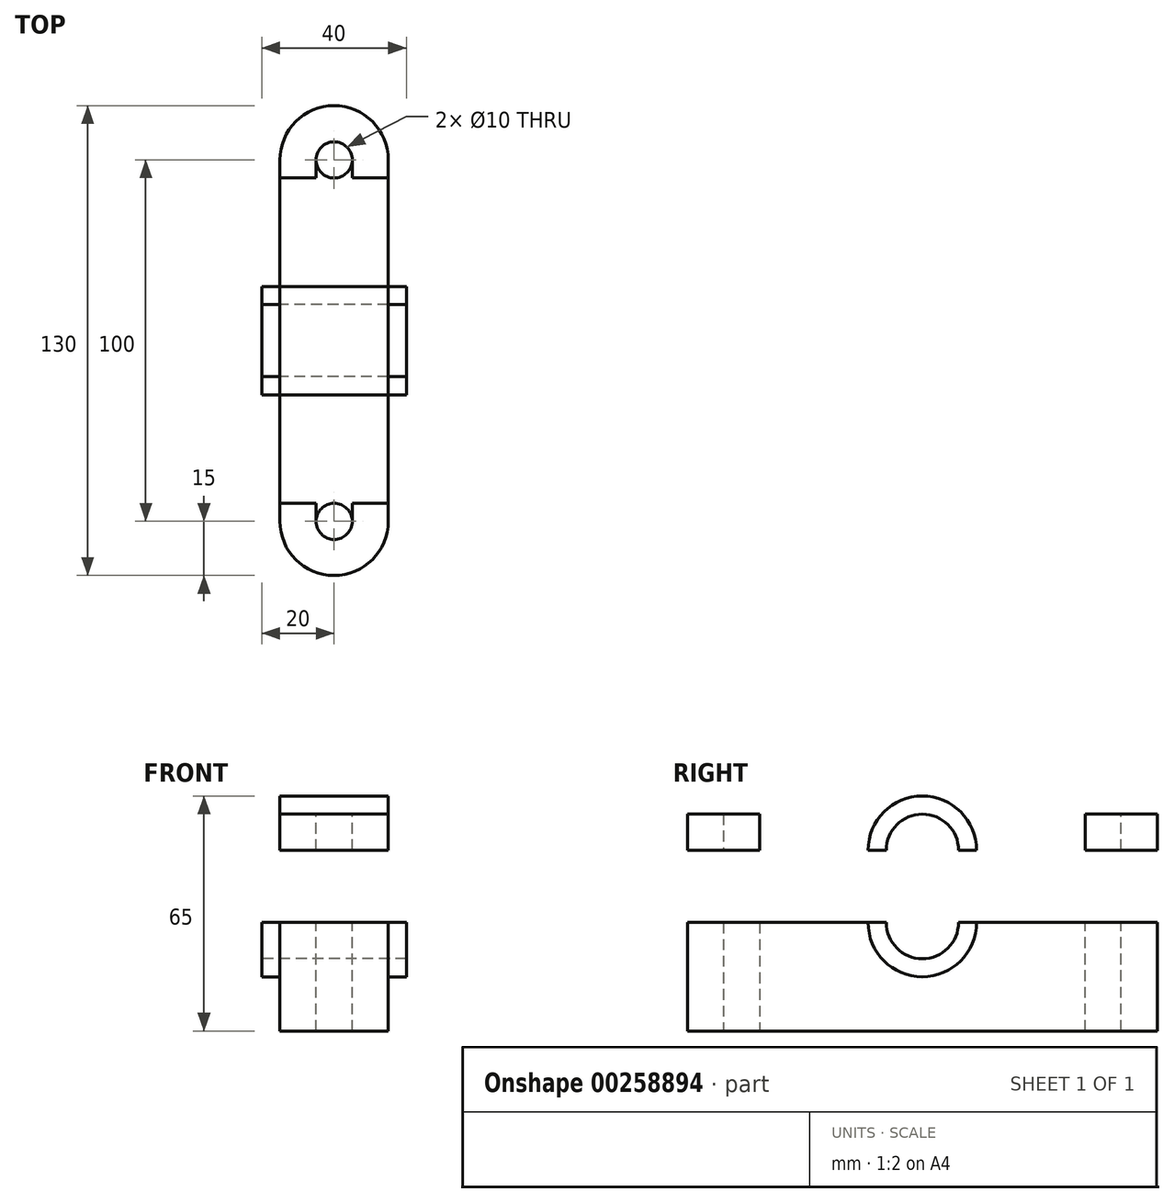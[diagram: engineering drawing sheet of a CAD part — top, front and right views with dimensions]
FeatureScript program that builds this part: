
annotation { "Feature Type Name" : "Feature", "Feature Type Description" : "" }
export const myFeature = defineFeature(function(context is Context, id is Id, definition is map)
    precondition{}
    {
        {
            var Q0;
            Q0=qCreatedBy(makeId("Right.planeOp"),FACE);
            var sketch = newSketch(context, id + "F0", { "sketchPlane" : qUnion([Q0])});
            skLineSegment(sketch, "E0", {"start": v(-65, 0) * mm, "end": v(-65, 30) * mm});
            skLineSegment(sketch, "E1", {"start": v(65, 0) * mm, "end": v(65, 30) * mm});
            skLineSegment(sketch, "E2", {"start": v(-50, 0) * mm, "end": v(-50, 30) * mm, "construction": true});
            skLineSegment(sketch, "E3", {"start": v(50, 0) * mm, "end": v(50, 30) * mm, "construction": true});
            skLineSegment(sketch, "E4.0", {"start": v(-45, 0) * mm, "end": v(-45, 30) * mm});
            skLineSegment(sketch, "E5.0", {"start": v(-55, 0) * mm, "end": v(-55, 30) * mm});
            skLineSegment(sketch, "E6.0", {"start": v(55, 0) * mm, "end": v(55, 30) * mm});
            skLineSegment(sketch, "E7.0", {"start": v(45, 0) * mm, "end": v(45, 30) * mm});
            skLineSegment(sketch, "E8", {"start": v(0, 0) * mm, "end": v(-45, 0) * mm});
            skLineSegment(sketch, "E9", {"start": v(-50, 0) * mm, "end": v(-45, 0) * mm});
            skLineSegment(sketch, "E10", {"start": v(-55, 0) * mm, "end": v(-50, 0) * mm});
            skLineSegment(sketch, "E11", {"start": v(-55, 0) * mm, "end": v(-65, 0) * mm});
            skLineSegment(sketch, "E12", {"start": v(-65, 30) * mm, "end": v(-55, 30) * mm});
            skLineSegment(sketch, "E13", {"start": v(-50, 30) * mm, "end": v(-55, 30) * mm});
            skLineSegment(sketch, "E14", {"start": v(-45, 30) * mm, "end": v(-50, 30) * mm});
            skLineSegment(sketch, "E15", {"start": v(-45, 30) * mm, "end": v(-15, 30) * mm});
            skArc(sketch, "E16", {"start": v(-10, 30) * mm, "mid": v(0, 20) * mm, "end": v(10, 30) * mm});
            skArc(sketch, "E17", {"start": v(-15, 30) * mm, "mid": v(0, 15) * mm, "end": v(15, 30) * mm});
            skLineSegment(sketch, "E18", {"start": v(-15, 30) * mm, "end": v(-10, 30) * mm});
            skLineSegment(sketch, "E19", {"start": v(10, 30) * mm, "end": v(15, 30) * mm});
            skLineSegment(sketch, "E20", {"start": v(15, 30) * mm, "end": v(45, 30) * mm});
            skLineSegment(sketch, "E21", {"start": v(50, 30) * mm, "end": v(45, 30) * mm});
            skLineSegment(sketch, "E22", {"start": v(55, 30) * mm, "end": v(50, 30) * mm});
            skLineSegment(sketch, "E23", {"start": v(55, 30) * mm, "end": v(65, 30) * mm});
            skLineSegment(sketch, "E24", {"start": v(55, 0) * mm, "end": v(65, 0) * mm});
            skLineSegment(sketch, "E25", {"start": v(50, 0) * mm, "end": v(55, 0) * mm});
            skLineSegment(sketch, "E26", {"start": v(45, 0) * mm, "end": v(50, 0) * mm});
            skLineSegment(sketch, "E27", {"start": v(0, 0) * mm, "end": v(45, 0) * mm});
            skArc(sketch, "E28", {"start": v(-10, 50) * mm, "mid": v(0, 60) * mm, "end": v(10, 50) * mm});
            skArc(sketch, "E29", {"start": v(-15, 50) * mm, "mid": v(0, 65) * mm, "end": v(15, 50) * mm});
            skLineSegment(sketch, "E30", {"start": v(-15, 50) * mm, "end": v(-10, 50) * mm});
            skLineSegment(sketch, "E31", {"start": v(10, 50) * mm, "end": v(15, 50) * mm});
            skArc(sketch, "E32", {"start": v(-28.28, 60) * mm, "mid": v(0, 80) * mm, "end": v(28.28, 60) * mm});
            skLineSegment(sketch, "E33", {"start": v(15, 50) * mm, "end": v(45, 50) * mm});
            skLineSegment(sketch, "E34", {"start": v(45, 50) * mm, "end": v(55, 50) * mm});
            skLineSegment(sketch, "E35", {"start": v(55, 50) * mm, "end": v(65, 50) * mm});
            skLineSegment(sketch, "E36", {"start": v(65, 50) * mm, "end": v(65, 60) * mm});
            skLineSegment(sketch, "E37", {"start": v(-15, 50) * mm, "end": v(-45, 50) * mm});
            skLineSegment(sketch, "E38", {"start": v(-45, 50) * mm, "end": v(-55, 50) * mm});
            skLineSegment(sketch, "E39", {"start": v(-55, 50) * mm, "end": v(-65, 50) * mm});
            skLineSegment(sketch, "E40", {"start": v(-65, 50) * mm, "end": v(-65, 60) * mm});
            skLineSegment(sketch, "E41", {"start": v(55, 50) * mm, "end": v(55, 60) * mm});
            skLineSegment(sketch, "E42", {"start": v(55, 60) * mm, "end": v(65, 60) * mm});
            skLineSegment(sketch, "E43", {"start": v(45, 50) * mm, "end": v(45, 60) * mm});
            skLineSegment(sketch, "E44", {"start": v(45, 60) * mm, "end": v(55, 60) * mm});
            skLineSegment(sketch, "E45", {"start": v(45, 60) * mm, "end": v(28.28, 60) * mm});
            skLineSegment(sketch, "E46", {"start": v(-55, 50) * mm, "end": v(-55, 60) * mm});
            skLineSegment(sketch, "E47", {"start": v(-55, 60) * mm, "end": v(-65, 60) * mm});
            skLineSegment(sketch, "E48", {"start": v(-45, 50) * mm, "end": v(-45, 60) * mm});
            skLineSegment(sketch, "E49", {"start": v(-45, 60) * mm, "end": v(-55, 60) * mm});
            skLineSegment(sketch, "E50", {"start": v(-45, 60) * mm, "end": v(-28.28, 60) * mm});
            skSolve(sketch);
        }
        {
            var Q0;
            Q0=makeQuery(id+"F0.imprint","IMPRINT",FACE,{"disambiguationData":[TD([[makeQuery(id+"F0.imprint","IMPRINT",EDGE,{"derivedFrom":sQuery(id+"F0.wireOp",EDGE,"E28")}),1.0]])]});
            var Q1;
            Q1=makeQuery(id+"F0.imprint","IMPRINT",FACE,{"disambiguationData":[TD([[makeQuery(id+"F0.imprint","IMPRINT",EDGE,{"derivedFrom":sQuery(id+"F0.wireOp",EDGE,"E16")}),-1.0]])]});
            extrude(context, id + "F1", {"entities" : qUnion([Q0, Q1]), "depth" : 40 * mm, "symmetric" : true});
        }
        {
            var Q0;
            Q0=makeQuery(id+"F0.imprint","IMPRINT",FACE,{"disambiguationData":[TD([[makeQuery(id+"F0.imprint","IMPRINT",EDGE,{"derivedFrom":sQuery(id+"F0.wireOp",EDGE,"E39")}),-1.0]])]});
            var Q1;
            Q1=makeQuery(id+"F0.imprint","IMPRINT",FACE,{"disambiguationData":[TD([[makeQuery(id+"F0.imprint","IMPRINT",EDGE,{"derivedFrom":sQuery(id+"F0.wireOp",EDGE,"E29")}),1.0]])]});
            var Q2;
            Q2=makeQuery(id+"F0.imprint","IMPRINT",FACE,{"disambiguationData":[TD([[makeQuery(id+"F0.imprint","IMPRINT",EDGE,{"derivedFrom":sQuery(id+"F0.wireOp",EDGE,"E38")}),-1.0]])]});
            var Q3;
            Q3=makeQuery(id+"F0.imprint","IMPRINT",FACE,{"disambiguationData":[TD([[makeQuery(id+"F0.imprint","IMPRINT",EDGE,{"derivedFrom":sQuery(id+"F0.wireOp",EDGE,"E34")}),1.0]])]});
            var Q4;
            Q4=makeQuery(id+"F0.imprint","IMPRINT",FACE,{"disambiguationData":[TD([[makeQuery(id+"F0.imprint","IMPRINT",EDGE,{"derivedFrom":sQuery(id+"F0.wireOp",EDGE,"E35")}),1.0]])]});
            var Q5;
            Q5=makeQuery(id+"F0.imprint","IMPRINT",FACE,{"disambiguationData":[TD([[makeQuery(id+"F0.imprint","IMPRINT",EDGE,{"derivedFrom":sQuery(id+"F0.wireOp",EDGE,"E4.0")}),-1.0]])]});
            var Q6;
            Q6=makeQuery(id+"F0.imprint","IMPRINT",FACE,{"disambiguationData":[TD([[makeQuery(id+"F0.imprint","IMPRINT",EDGE,{"derivedFrom":sQuery(id+"F0.wireOp",EDGE,"E6.0")}),1.0]])]});
            var Q7;
            Q7=makeQuery(id+"F0.imprint","IMPRINT",FACE,{"disambiguationData":[TD([[makeQuery(id+"F0.imprint","IMPRINT",EDGE,{"derivedFrom":sQuery(id+"F0.wireOp",EDGE,"E1")}),1.0]])]});
            var Q8;
            Q8=makeQuery(id+"F0.imprint","IMPRINT",FACE,{"disambiguationData":[TD([[makeQuery(id+"F0.imprint","IMPRINT",EDGE,{"derivedFrom":sQuery(id+"F0.wireOp",EDGE,"E4.0")}),1.0]])]});
            var Q9;
            Q9=makeQuery(id+"F0.imprint","IMPRINT",FACE,{"disambiguationData":[TD([[makeQuery(id+"F0.imprint","IMPRINT",EDGE,{"derivedFrom":sQuery(id+"F0.wireOp",EDGE,"E0")}),-1.0]])]});
            extrude(context, id + "F2", {"entities" : qUnion([Q0, Q1, Q2, Q3, Q4, Q5, Q6, Q7, Q8, Q9]), "operationType" : NewBodyOperationType.ADD, "depth" : 30 * mm, "symmetric" : true});
        }
        {
            var Q0;
            Q0=makeQuery(id+"F0.imprint","IMPRINT",FACE,{"disambiguationData":[TD([[makeQuery(id+"F0.imprint","IMPRINT",EDGE,{"derivedFrom":sQuery(id+"F0.wireOp",EDGE,"E38")}),-1.0]])]});
            var Q1;
            Q1=makeQuery(id+"F0.imprint","IMPRINT",FACE,{"disambiguationData":[TD([[makeQuery(id+"F0.imprint","IMPRINT",EDGE,{"derivedFrom":sQuery(id+"F0.wireOp",EDGE,"E4.0")}),1.0]])]});
            var Q2;
            Q2=makeQuery(id+"F0.imprint","IMPRINT",FACE,{"disambiguationData":[TD([[makeQuery(id+"F0.imprint","IMPRINT",EDGE,{"derivedFrom":sQuery(id+"F0.wireOp",EDGE,"E34")}),1.0]])]});
            var Q3;
            Q3=makeQuery(id+"F0.imprint","IMPRINT",FACE,{"disambiguationData":[TD([[makeQuery(id+"F0.imprint","IMPRINT",EDGE,{"derivedFrom":sQuery(id+"F0.wireOp",EDGE,"E6.0")}),1.0]])]});
            extrude(context, id + "F3", {"entities" : qUnion([Q0, Q1, Q2, Q3]), "operationType" : NewBodyOperationType.REMOVE, "oppositeDirection" : true, "depth" : 10 * mm, "symmetric" : true});
        }
        {
            var Q0;
            Q0=makeQuery(id+"F3.boolean.opBoolean","COPY",EDGE,{"derivedFrom":makeQuery(id+"F3.opExtrude","CAP_EDGE",EDGE,{"disambiguationData":[OSD([sQuery(id+"F0.wireOp",EDGE,"E48")])],"isStart":false})});
            var Q1;
            Q1=makeQuery(id+"F3.boolean.opBoolean","COPY",EDGE,{"derivedFrom":makeQuery(id+"F3.opExtrude","CAP_EDGE",EDGE,{"disambiguationData":[OSD([sQuery(id+"F0.wireOp",EDGE,"E41")])],"isStart":false})});
            var Q2;
            Q2=makeQuery(id+"F3.boolean.opBoolean","COPY",EDGE,{"derivedFrom":makeQuery(id+"F3.opExtrude","CAP_EDGE",EDGE,{"disambiguationData":[OSD([sQuery(id+"F0.wireOp",EDGE,"E6.0")])],"isStart":false})});
            var Q3;
            Q3=makeQuery(id+"F3.boolean.opBoolean","COPY",EDGE,{"derivedFrom":makeQuery(id+"F3.opExtrude","CAP_EDGE",EDGE,{"disambiguationData":[OSD([sQuery(id+"F0.wireOp",EDGE,"E4.0")])],"isStart":false})});
            var Q4;
            Q4=makeQuery(id+"F3.boolean.opBoolean","COPY",EDGE,{"derivedFrom":makeQuery(id+"F3.opExtrude","CAP_EDGE",EDGE,{"disambiguationData":[OSD([sQuery(id+"F0.wireOp",EDGE,"E5.0")])],"isStart":false})});
            var Q5;
            Q5=makeQuery(id+"F3.boolean.opBoolean","COPY",EDGE,{"derivedFrom":makeQuery(id+"F3.opExtrude","CAP_EDGE",EDGE,{"disambiguationData":[OSD([sQuery(id+"F0.wireOp",EDGE,"E46")])],"isStart":false})});
            var Q6;
            Q6=makeQuery(id+"F3.boolean.opBoolean","COPY",EDGE,{"derivedFrom":makeQuery(id+"F3.opExtrude","CAP_EDGE",EDGE,{"disambiguationData":[OSD([sQuery(id+"F0.wireOp",EDGE,"E43")])],"isStart":false})});
            var Q7;
            Q7=makeQuery(id+"F3.boolean.opBoolean","COPY",EDGE,{"derivedFrom":makeQuery(id+"F3.opExtrude","CAP_EDGE",EDGE,{"disambiguationData":[OSD([sQuery(id+"F0.wireOp",EDGE,"E7.0")])],"isStart":false})});
            var Q8;
            Q8=makeQuery(id+"F3.boolean.opBoolean","COPY",EDGE,{"derivedFrom":makeQuery(id+"F3.opExtrude","CAP_EDGE",EDGE,{"disambiguationData":[OSD([sQuery(id+"F0.wireOp",EDGE,"E46")])],"isStart":true})});
            var Q9;
            Q9=makeQuery(id+"F3.boolean.opBoolean","COPY",EDGE,{"derivedFrom":makeQuery(id+"F3.opExtrude","CAP_EDGE",EDGE,{"disambiguationData":[OSD([sQuery(id+"F0.wireOp",EDGE,"E43")])],"isStart":true})});
            var Q10;
            Q10=makeQuery(id+"F3.boolean.opBoolean","COPY",EDGE,{"derivedFrom":makeQuery(id+"F3.opExtrude","CAP_EDGE",EDGE,{"disambiguationData":[OSD([sQuery(id+"F0.wireOp",EDGE,"E41")])],"isStart":true})});
            var Q11;
            Q11=makeQuery(id+"F3.boolean.opBoolean","COPY",EDGE,{"derivedFrom":makeQuery(id+"F3.opExtrude","CAP_EDGE",EDGE,{"disambiguationData":[OSD([sQuery(id+"F0.wireOp",EDGE,"E48")])],"isStart":true})});
            var Q12;
            Q12=makeQuery(id+"F3.boolean.opBoolean","COPY",EDGE,{"derivedFrom":makeQuery(id+"F3.opExtrude","CAP_EDGE",EDGE,{"disambiguationData":[OSD([sQuery(id+"F0.wireOp",EDGE,"E5.0")])],"isStart":true})});
            var Q13;
            Q13=makeQuery(id+"F3.boolean.opBoolean","COPY",EDGE,{"derivedFrom":makeQuery(id+"F3.opExtrude","CAP_EDGE",EDGE,{"disambiguationData":[OSD([sQuery(id+"F0.wireOp",EDGE,"E4.0")])],"isStart":true})});
            var Q14;
            Q14=makeQuery(id+"F3.boolean.opBoolean","COPY",EDGE,{"derivedFrom":makeQuery(id+"F3.opExtrude","CAP_EDGE",EDGE,{"disambiguationData":[OSD([sQuery(id+"F0.wireOp",EDGE,"E6.0")])],"isStart":true})});
            var Q15;
            Q15=makeQuery(id+"F3.boolean.opBoolean","COPY",EDGE,{"derivedFrom":makeQuery(id+"F3.opExtrude","CAP_EDGE",EDGE,{"disambiguationData":[OSD([sQuery(id+"F0.wireOp",EDGE,"E7.0")])],"isStart":true})});
            fillet(context, id + "F4", {"entities" : qUnion([Q0, Q1, Q2, Q3, Q4, Q5, Q6, Q7, Q8, Q9, Q10, Q11, Q12, Q13, Q14, Q15]), "radius" : 5 * mm, "tangentPropagation" : true, "allowEdgeOverflow" : false});
        }
        {
            var Q0;
            Q0=makeQuery(id+"F2.opExtrude","CAP_EDGE",EDGE,{"disambiguationData":[OSD([sQuery(id+"F0.wireOp",EDGE,"E0")])],"isStart":false});
            var Q1;
            Q1=makeQuery(id+"F2.opExtrude","CAP_EDGE",EDGE,{"disambiguationData":[OSD([sQuery(id+"F0.wireOp",EDGE,"E0")])],"isStart":true});
            var Q2;
            Q2=makeQuery(id+"F2.opExtrude","CAP_EDGE",EDGE,{"disambiguationData":[OSD([sQuery(id+"F0.wireOp",EDGE,"E40")])],"isStart":true});
            var Q3;
            Q3=makeQuery(id+"F2.opExtrude","CAP_EDGE",EDGE,{"disambiguationData":[OSD([sQuery(id+"F0.wireOp",EDGE,"E40")])],"isStart":false});
            var Q4;
            Q4=makeQuery(id+"F2.opExtrude","CAP_EDGE",EDGE,{"disambiguationData":[OSD([sQuery(id+"F0.wireOp",EDGE,"E36")])],"isStart":false});
            var Q5;
            Q5=makeQuery(id+"F2.opExtrude","CAP_EDGE",EDGE,{"disambiguationData":[OSD([sQuery(id+"F0.wireOp",EDGE,"E1")])],"isStart":false});
            var Q6;
            Q6=makeQuery(id+"F2.opExtrude","CAP_EDGE",EDGE,{"disambiguationData":[OSD([sQuery(id+"F0.wireOp",EDGE,"E1")])],"isStart":true});
            var Q7;
            Q7=makeQuery(id+"F2.opExtrude","CAP_EDGE",EDGE,{"disambiguationData":[OSD([sQuery(id+"F0.wireOp",EDGE,"E36")])],"isStart":true});
            fillet(context, id + "F5", {"entities" : qUnion([Q0, Q1, Q2, Q3, Q4, Q5, Q6, Q7]), "radius" : 15 * mm, "tangentPropagation" : true, "allowEdgeOverflow" : false});
        }
    });
